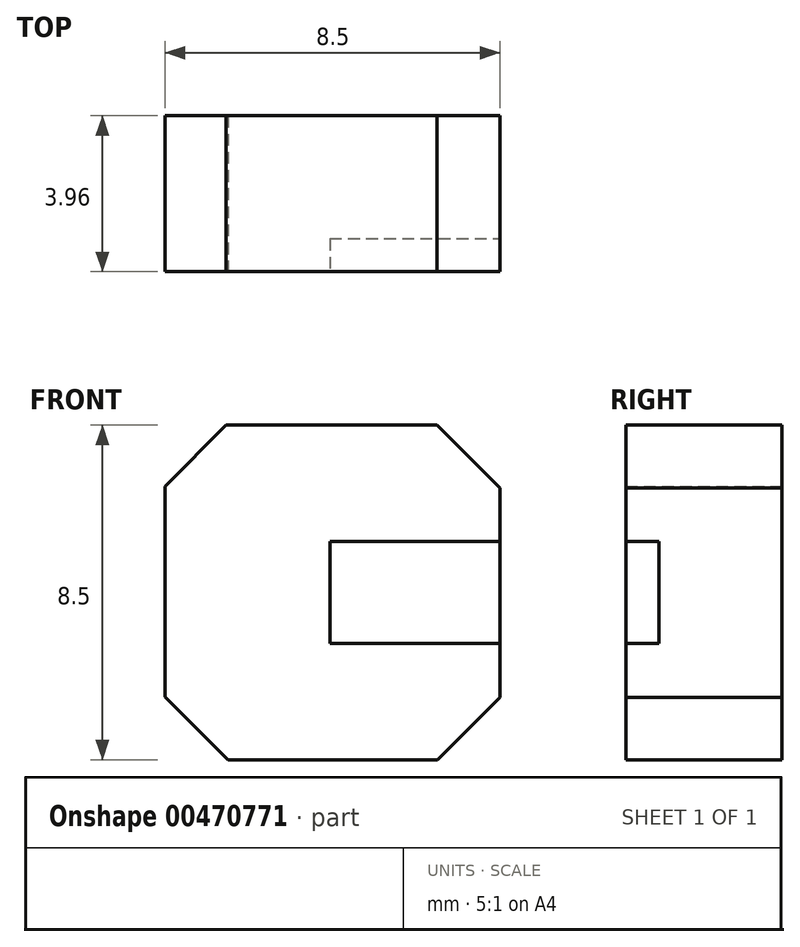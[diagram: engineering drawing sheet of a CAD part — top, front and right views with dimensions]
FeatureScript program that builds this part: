
annotation { "Feature Type Name" : "Feature", "Feature Type Description" : "" }
export const myFeature = defineFeature(function(context is Context, id is Id, definition is map)
    precondition{}
    {
        {
            var Q0;
            Q0=qCreatedBy(makeId("Front.planeOp"),FACE);
            var sketch = newSketch(context, id + "F0", { "sketchPlane" : qUnion([Q0])});
            skLineSegment(sketch, "E0.bottom", {"start": v(4.25, -4.25) * mm, "end": v(-4.25, -4.25) * mm});
            skLineSegment(sketch, "E0.top", {"start": v(4.25, 4.25) * mm, "end": v(-4.25, 4.25) * mm});
            skLineSegment(sketch, "E0.left", {"start": v(4.25, -4.25) * mm, "end": v(4.25, 4.25) * mm});
            skLineSegment(sketch, "E0.right", {"start": v(-4.25, -4.25) * mm, "end": v(-4.25, 4.25) * mm});
            skPoint(sketch, "E0.middle", {"position": v(0, 0) * mm});
            skSolve(sketch);
        }
        {
            var Q0;
            Q0=makeQuery(id+"F0.imprint","IMPRINT",FACE,{"disambiguationData":[TD([[makeQuery(id+"F0.imprint","IMPRINT",EDGE,{"derivedFrom":sQuery(id+"F0.wireOp",EDGE,"E0.bottom")}),-1.0]])]});
            var sketch = newSketch(context, id + "F1", { "sketchPlane" : qUnion([Q0])});
            skLineSegment(sketch, "E1", {"start": v(-4.25, 2.68) * mm, "end": v(-2.68, 4.28) * mm});
            skLineSegment(sketch, "E2", {"start": v(-4.28, 4.28) * mm, "end": v(-4.25, 2.68) * mm});
            skLineSegment(sketch, "E3", {"start": v(-2.68, 4.28) * mm, "end": v(-4.28, 4.28) * mm});
            skSolve(sketch);
        }
        {
            var Q0;
            Q0=makeQuery(id+"F0.imprint","IMPRINT",FACE,{"disambiguationData":[TD([[makeQuery(id+"F0.imprint","IMPRINT",EDGE,{"derivedFrom":sQuery(id+"F0.wireOp",EDGE,"E0.bottom")}),-1.0]])]});
            extrude(context, id + "F2", {"entities" : qUnion([Q0]), "depth" : 3.96 * mm});
        }
        {
            var Q0;
            Q0 = qSketchRegion(id + "F1", true);
            extrude(context, id + "F3", {"entities" : qUnion([Q0]), "operationType" : NewBodyOperationType.REMOVE, "depth" : 4.3 * mm});
        }
        {
            var Q0;
            Q0=makeQuery(id+"F2.opExtrude","CAP_FACE",FACE,{"disambiguationData":[OSD([sQuery(id+"F0.wireOp",EDGE,"E0.bottom"),sQuery(id+"F0.wireOp",EDGE,"E0.top"),sQuery(id+"F0.wireOp",EDGE,"E0.left"),sQuery(id+"F0.wireOp",EDGE,"E0.right")])],"isStart":false});
            var sketch = newSketch(context, id + "F4", { "sketchPlane" : qUnion([Q0])});
            skLineSegment(sketch, "E4", {"start": v(2.65, 4.25) * mm, "end": v(4.25, 2.65) * mm});
            skLineSegment(sketch, "E5", {"start": v(4.25, 2.65) * mm, "end": v(4.25, 4.25) * mm});
            skLineSegment(sketch, "E6", {"start": v(4.25, 4.25) * mm, "end": v(2.65, 4.25) * mm});
            skSolve(sketch);
        }
        {
            var Q0;
            Q0 = qSketchRegion(id + "F4", true);
            extrude(context, id + "F5", {"entities" : qUnion([Q0]), "operationType" : NewBodyOperationType.REMOVE, "oppositeDirection" : true, "depth" : 4.57 * mm});
        }
        {
            var Q0;
            Q0=makeQuery(id+"F2.opExtrude","CAP_FACE",FACE,{"disambiguationData":[OSD([sQuery(id+"F0.wireOp",EDGE,"E0.bottom"),sQuery(id+"F0.wireOp",EDGE,"E0.top"),sQuery(id+"F0.wireOp",EDGE,"E0.left"),sQuery(id+"F0.wireOp",EDGE,"E0.right")])],"isStart":false});
            var sketch = newSketch(context, id + "F6", { "sketchPlane" : qUnion([Q0])});
            skLineSegment(sketch, "E7", {"start": v(-4.25, -4.25) * mm, "end": v(-4.25, -2.65) * mm});
            skLineSegment(sketch, "E8", {"start": v(-4.25, -2.65) * mm, "end": v(-2.65, -4.25) * mm});
            skLineSegment(sketch, "E9", {"start": v(-2.65, -4.25) * mm, "end": v(-4.25, -4.25) * mm});
            skSolve(sketch);
        }
        {
            var Q0;
            Q0 = qSketchRegion(id + "F6", true);
            extrude(context, id + "F7", {"entities" : qUnion([Q0]), "operationType" : NewBodyOperationType.REMOVE, "oppositeDirection" : true, "depth" : 25.4 * mm});
        }
        {
            var Q0;
            Q0=makeQuery(id+"F2.opExtrude","CAP_FACE",FACE,{"disambiguationData":[OSD([sQuery(id+"F0.wireOp",EDGE,"E0.bottom"),sQuery(id+"F0.wireOp",EDGE,"E0.top"),sQuery(id+"F0.wireOp",EDGE,"E0.left"),sQuery(id+"F0.wireOp",EDGE,"E0.right")])],"isStart":false});
            var sketch = newSketch(context, id + "F8", { "sketchPlane" : qUnion([Q0])});
            skLineSegment(sketch, "E10", {"start": v(4.25, -4.25) * mm, "end": v(4.25, -2.67) * mm});
            skLineSegment(sketch, "E11", {"start": v(4.25, -2.67) * mm, "end": v(2.67, -4.25) * mm});
            skLineSegment(sketch, "E12", {"start": v(2.67, -4.25) * mm, "end": v(4.25, -4.25) * mm});
            skSolve(sketch);
        }
        {
            var Q0;
            Q0 = qSketchRegion(id + "F8", true);
            extrude(context, id + "F9", {"entities" : qUnion([Q0]), "operationType" : NewBodyOperationType.REMOVE, "oppositeDirection" : true, "depth" : 25.4 * mm});
        }
        {
            var Q0;
            Q0=makeQuery(id+"F2.opExtrude","SWEPT_FACE",FACE,{"disambiguationData":[OSD([sQuery(id+"F0.wireOp",EDGE,"E0.left")])]});
            var sketch = newSketch(context, id + "F10", { "sketchPlane" : qUnion([Q0])});
            skLineSegment(sketch, "E13.bottom", {"start": v(-3.12, -1.3) * mm, "end": v(-4.14, -1.3) * mm});
            skLineSegment(sketch, "E13.top", {"start": v(-3.12, 1.3) * mm, "end": v(-4.14, 1.3) * mm});
            skLineSegment(sketch, "E13.left", {"start": v(-3.12, -1.3) * mm, "end": v(-3.12, 1.3) * mm});
            skLineSegment(sketch, "E13.right", {"start": v(-4.14, -1.3) * mm, "end": v(-4.14, 1.3) * mm});
            skPoint(sketch, "E13.middle", {"position": v(-3.63, 0) * mm});
            skSolve(sketch);
        }
        {
            var Q0;
            Q0 = qSketchRegion(id + "F10", true);
            extrude(context, id + "F11", {"entities" : qUnion([Q0]), "operationType" : NewBodyOperationType.REMOVE, "oppositeDirection" : true, "depth" : 4.32 * mm});
        }
    });
